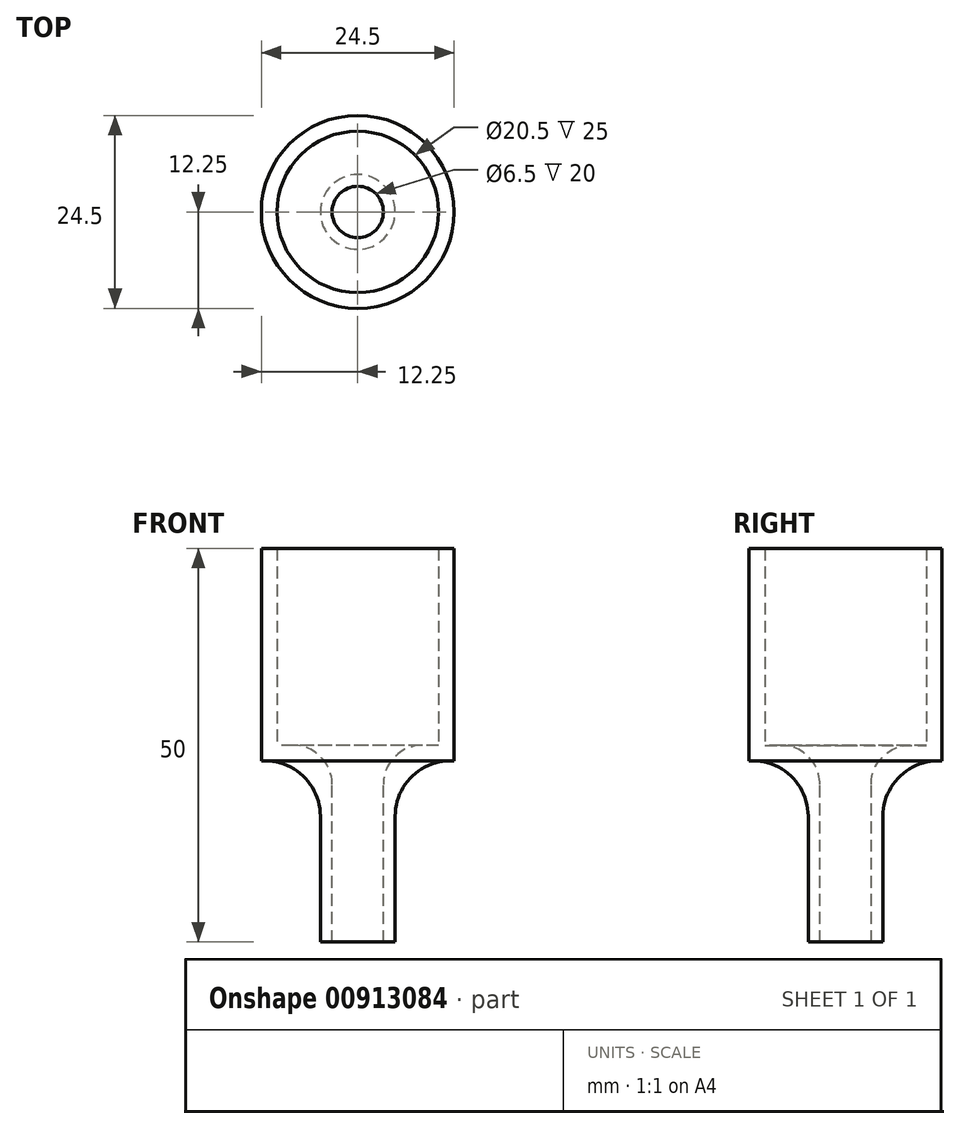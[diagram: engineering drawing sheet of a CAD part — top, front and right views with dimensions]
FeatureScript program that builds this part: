
annotation { "Feature Type Name" : "Feature", "Feature Type Description" : "" }
export const myFeature = defineFeature(function(context is Context, id is Id, definition is map)
    precondition{}
    {
        {
            var Q0;
            Q0=qCreatedBy(makeId("Top.planeOp"),FACE);
            var sketch = newSketch(context, id + "F0", { "sketchPlane" : qUnion([Q0])});
            skCircle(sketch, "E0", {"center": v(0, 0) * mm, "radius": 10.25 * mm});
            skCircle(sketch, "E1", {"center": v(0, 0) * mm, "radius": 12.25 * mm});
            skCircle(sketch, "E2", {"center": v(0, 0) * mm, "radius": 4.75 * mm});
            skCircle(sketch, "E3", {"center": v(0, 0) * mm, "radius": 3.25 * mm});
            skSolve(sketch);
        }
        {
            var Q0;
            Q0 = qSketchRegion(id + "F0", true);
            extrude(context, id + "F1", {"entities" : qUnion([Q0]), "depth" : 25 * mm, "offsetDistance" : 25 * mm});
        }
        {
            var Q0;
            Q0=makeQuery(id+"F0.imprint","IMPRINT",FACE,{"disambiguationData":[TD([[makeQuery(id+"F0.imprint","IMPRINT",EDGE,{"derivedFrom":sQuery(id+"F0.wireOp",EDGE,"E0")}),1.0]])]});
            var Q1;
            Q1=makeQuery(id+"F0.imprint","IMPRINT",FACE,{"disambiguationData":[TD([[makeQuery(id+"F0.imprint","IMPRINT",EDGE,{"derivedFrom":sQuery(id+"F0.wireOp",EDGE,"E0")}),-1.0]])]});
            var Q2;
            Q2=makeQuery(id+"F0.imprint","IMPRINT",FACE,{"disambiguationData":[TD([[makeQuery(id+"F0.imprint","IMPRINT",EDGE,{"derivedFrom":sQuery(id+"F0.wireOp",EDGE,"E2")}),1.0]])]});
            extrude(context, id + "F2", {"entities" : qUnion([Q0, Q1, Q2]), "operationType" : NewBodyOperationType.ADD, "oppositeDirection" : true, "depth" : 2 * mm, "offsetDistance" : 25 * mm});
        }
        {
            var Q0;
            Q0=makeQuery(id+"F0.imprint","IMPRINT",FACE,{"disambiguationData":[TD([[makeQuery(id+"F0.imprint","IMPRINT",EDGE,{"derivedFrom":sQuery(id+"F0.wireOp",EDGE,"E2")}),1.0]])]});
            extrude(context, id + "F3", {"entities" : qUnion([Q0]), "operationType" : NewBodyOperationType.ADD, "oppositeDirection" : true, "depth" : 25 * mm, "offsetDistance" : 25 * mm});
        }
        {
            var Q0;
            Q0=makeQuery(id+"F3.boolean.opBoolean","INTERSECT",EDGE,{"derivedFrom":[makeQuery(id+"F2.opExtrude","CAP_FACE",FACE,{"disambiguationData":[OSD([sQuery(id+"F0.wireOp",EDGE,"E1"),sQuery(id+"F0.wireOp",EDGE,"E3")])],"isStart":false}),makeQuery(id+"F3.opExtrude","SWEPT_FACE",FACE,{"disambiguationData":[OSD([sQuery(id+"F0.wireOp",EDGE,"E2")])]})]});
            fillet(context, id + "F4", {"entities" : qUnion([Q0]), "radius" : 7 * mm, "tangentPropagation" : true, "allowEdgeOverflow" : false});
        }
        {
            var Q0;
            Q0=makeQuery(id+"F2.opExtrude","CAP_EDGE",EDGE,{"disambiguationData":[OSD([sQuery(id+"F0.wireOp",EDGE,"E3")])],"isStart":true});
            fillet(context, id + "F5", {"entities" : qUnion([Q0]), "radius" : 5 * mm, "tangentPropagation" : true, "allowEdgeOverflow" : false});
        }
    });
